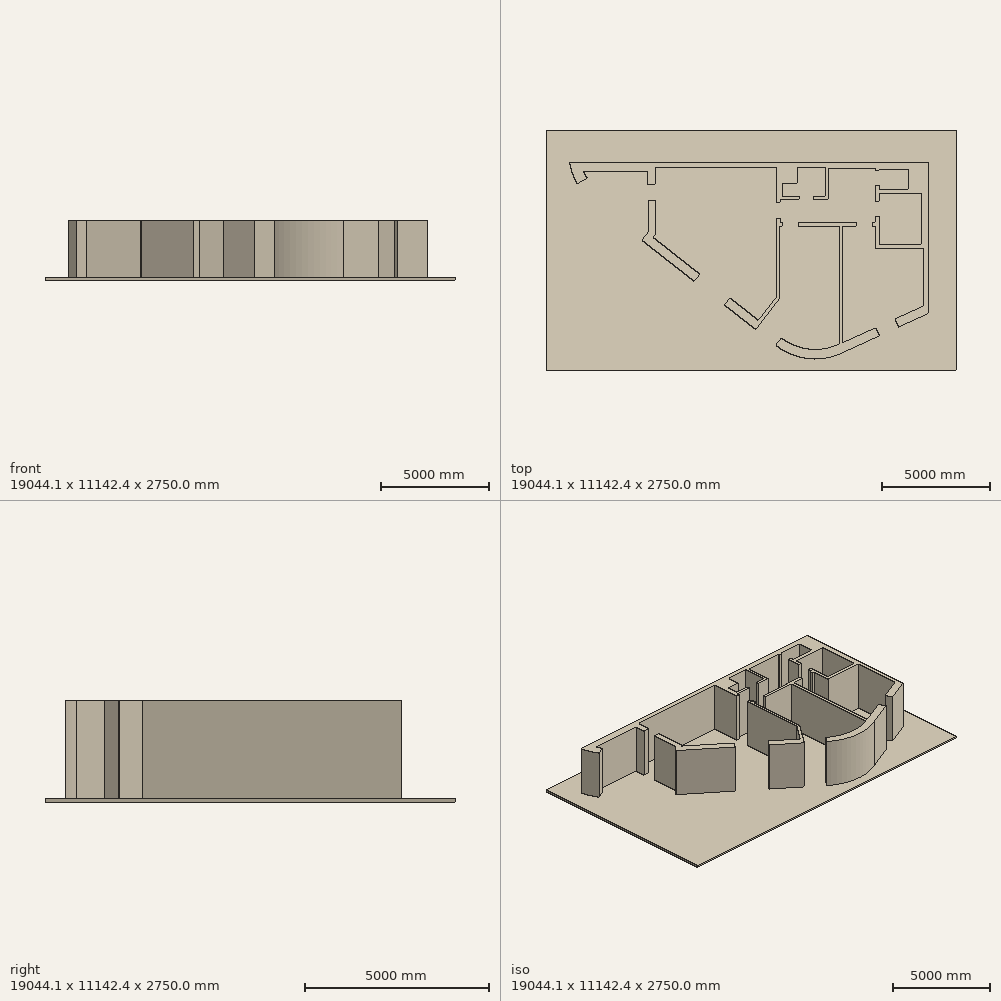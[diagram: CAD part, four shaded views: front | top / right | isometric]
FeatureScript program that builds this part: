
annotation { "Feature Type Name" : "Feature", "Feature Type Description" : "" }
export const myFeature = defineFeature(function(context is Context, id is Id, definition is map)
    precondition{}
    {
        {
            var Q0;
            Q0=qCreatedBy(makeId("Top.planeOp"),FACE);
            var sketch = newSketch(context, id + "F0", { "sketchPlane" : qUnion([Q0])});
            skLineSegment(sketch, "E0.bottom", {"start": v(-9332.98, 0) * mm, "end": v(-28377.12, 0) * mm});
            skLineSegment(sketch, "E0.top", {"start": v(-9332.98, 11142.35) * mm, "end": v(-28377.12, 11142.35) * mm});
            skLineSegment(sketch, "E0.left", {"start": v(-9332.98, 0) * mm, "end": v(-9332.98, 11142.35) * mm});
            skLineSegment(sketch, "E0.right", {"start": v(-28377.12, 0) * mm, "end": v(-28377.12, 11142.35) * mm});
            skSolve(sketch);
        }
        {
            var Q0;
            Q0=qCreatedBy(makeId("Top.planeOp"),FACE);
            var sketch = newSketch(context, id + "F1", { "sketchPlane" : qUnion([Q0])});
            skLineSegment(sketch, "E1", {"start": v(-17695.4, 9406.52) * mm, "end": v(-17695.4, 0) * mm, "construction": true});
            skLineSegment(sketch, "E2", {"start": v(-23335.4, 9420.42) * mm, "end": v(-23335.4, 0) * mm, "construction": true});
            skLineSegment(sketch, "E3", {"start": v(-26483.5, 8921.22) * mm, "end": v(-26661.71, 9232.56) * mm});
            skLineSegment(sketch, "E4", {"start": v(-26661.71, 9232.56) * mm, "end": v(-23679.3, 9232.56) * mm});
            skLineSegment(sketch, "E5", {"start": v(-23679.3, 9232.56) * mm, "end": v(-23679.3, 8644.23) * mm});
            skLineSegment(sketch, "E6", {"start": v(-23679.3, 8644.23) * mm, "end": v(-23335.4, 8644.23) * mm});
            skLineSegment(sketch, "E7", {"start": v(-23335.4, 8644.23) * mm, "end": v(-23335.4, 9420.42) * mm});
            skLineSegment(sketch, "E8", {"start": v(-23335.4, 9420.42) * mm, "end": v(-17884.5, 9420.42) * mm});
            skLineSegment(sketch, "E9", {"start": v(-17884.5, 9420.42) * mm, "end": v(-17695.4, 9420.42) * mm});
            skLineSegment(sketch, "E10", {"start": v(-26483.5, 8921.22) * mm, "end": v(-26938.35, 8660.86) * mm});
            skLineSegment(sketch, "E11", {"start": v(-23941.22, 6039.53) * mm, "end": v(-23657.8, 6399.56) * mm});
            skLineSegment(sketch, "E12", {"start": v(-23657.8, 6399.56) * mm, "end": v(-23657.8, 7903.53) * mm});
            skLineSegment(sketch, "E13", {"start": v(-23657.8, 7903.53) * mm, "end": v(-23335.4, 7903.53) * mm});
            skLineSegment(sketch, "E14", {"start": v(-23335.4, 7903.53) * mm, "end": v(-23335.4, 6259.12) * mm});
            skLineSegment(sketch, "E15", {"start": v(-23335.4, 6259.12) * mm, "end": v(-23412.66, 6169.75) * mm});
            skLineSegment(sketch, "E16", {"start": v(-23412.66, 6169.75) * mm, "end": v(-18525.74, 2320.29) * mm});
            skLineSegment(sketch, "E17", {"start": v(-18525.74, 2320.29) * mm, "end": v(-17695.4, 3390.84) * mm});
            skLineSegment(sketch, "E18", {"start": v(-17695.4, 3390.84) * mm, "end": v(-17695.4, 7043.86) * mm});
            skLineSegment(sketch, "E19", {"start": v(-17695.4, 7043.86) * mm, "end": v(-17529.29, 7043.86) * mm});
            skLineSegment(sketch, "E20", {"start": v(-17529.29, 7043.86) * mm, "end": v(-17529.29, 6860) * mm});
            skLineSegment(sketch, "E21", {"start": v(-17529.29, 6860) * mm, "end": v(-17434.81, 6860) * mm});
            skLineSegment(sketch, "E22", {"start": v(-17434.81, 6860) * mm, "end": v(-17434.81, 6678.72) * mm});
            skLineSegment(sketch, "E23", {"start": v(-17434.81, 6678.72) * mm, "end": v(-17531.84, 6678.72) * mm});
            skLineSegment(sketch, "E24", {"start": v(-17531.84, 6678.72) * mm, "end": v(-17531.84, 3343.08) * mm});
            skLineSegment(sketch, "E25", {"start": v(-17531.84, 3343.08) * mm, "end": v(-18647.56, 1890.31) * mm});
            skLineSegment(sketch, "E26", {"start": v(-18647.56, 1890.31) * mm, "end": v(-23941.22, 6039.53) * mm});
            skLineSegment(sketch, "E27", {"start": v(-17460.85, 1503.1) * mm, "end": v(-17728.59, 1163.2) * mm});
            skLineSegment(sketch, "E28", {"start": v(-14768.9, 6697.75) * mm, "end": v(-16661, 6697.75) * mm});
            skLineSegment(sketch, "E29", {"start": v(-16661, 6697.75) * mm, "end": v(-16661, 6850.95) * mm});
            skLineSegment(sketch, "E30", {"start": v(-16661, 6850.95) * mm, "end": v(-13976.46, 6865.49) * mm});
            skLineSegment(sketch, "E31", {"start": v(-13976.46, 6865.49) * mm, "end": v(-13975.51, 6690.41) * mm});
            skLineSegment(sketch, "E32", {"start": v(-13975.51, 6690.41) * mm, "end": v(-14608.4, 6690.41) * mm});
            skLineSegment(sketch, "E33", {"start": v(-14608.4, 6690.41) * mm, "end": v(-14608.4, 1282.42) * mm});
            skLineSegment(sketch, "E34", {"start": v(-14608.4, 1282.42) * mm, "end": v(-10858.67, 2988.86) * mm});
            skLineSegment(sketch, "E35", {"start": v(-10858.67, 2988.86) * mm, "end": v(-10858.67, 5686.8) * mm});
            skLineSegment(sketch, "E36", {"start": v(-10858.67, 5686.8) * mm, "end": v(-13106.53, 5686.8) * mm});
            skLineSegment(sketch, "E37", {"start": v(-13106.53, 5686.8) * mm, "end": v(-13106.53, 6690.41) * mm});
            skLineSegment(sketch, "E38", {"start": v(-13106.53, 6690.41) * mm, "end": v(-13212.43, 6690.41) * mm});
            skLineSegment(sketch, "E39", {"start": v(-13212.43, 6690.41) * mm, "end": v(-13212.43, 6866.77) * mm});
            skLineSegment(sketch, "E40", {"start": v(-13212.43, 6866.77) * mm, "end": v(-13094.97, 6866.77) * mm});
            skLineSegment(sketch, "E41", {"start": v(-13094.97, 6866.77) * mm, "end": v(-13094.97, 7134.88) * mm});
            skLineSegment(sketch, "E42", {"start": v(-13094.97, 7134.88) * mm, "end": v(-12918.79, 7134.88) * mm});
            skLineSegment(sketch, "E43", {"start": v(-12918.79, 7134.88) * mm, "end": v(-12918.79, 5870.93) * mm});
            skLineSegment(sketch, "E44", {"start": v(-12918.79, 5870.93) * mm, "end": v(-10960.3, 5870.93) * mm});
            skLineSegment(sketch, "E45", {"start": v(-10960.3, 5870.93) * mm, "end": v(-10960.3, 8217.53) * mm});
            skLineSegment(sketch, "E46", {"start": v(-10960.3, 8217.53) * mm, "end": v(-12926.45, 8217.53) * mm});
            skLineSegment(sketch, "E47", {"start": v(-12926.45, 8217.53) * mm, "end": v(-12926.45, 7847.28) * mm});
            skLineSegment(sketch, "E48", {"start": v(-12926.45, 7847.28) * mm, "end": v(-13094.97, 7847.28) * mm});
            skLineSegment(sketch, "E49", {"start": v(-13094.97, 7847.28) * mm, "end": v(-13094.97, 8592.88) * mm});
            skLineSegment(sketch, "E50", {"start": v(-13094.97, 8592.88) * mm, "end": v(-12923.9, 8592.88) * mm});
            skLineSegment(sketch, "E51", {"start": v(-12923.9, 8592.88) * mm, "end": v(-12923.9, 8409.04) * mm});
            skLineSegment(sketch, "E52", {"start": v(-12923.9, 8409.04) * mm, "end": v(-11542.5, 8409.04) * mm});
            skLineSegment(sketch, "E53", {"start": v(-11542.5, 8409.04) * mm, "end": v(-11542.5, 9343.6) * mm});
            skLineSegment(sketch, "E54", {"start": v(-11542.5, 9343.6) * mm, "end": v(-12923.9, 9343.6) * mm});
            skLineSegment(sketch, "E55", {"start": v(-12923.9, 9343.6) * mm, "end": v(-12923.9, 9266.99) * mm});
            skLineSegment(sketch, "E56", {"start": v(-12923.9, 9266.99) * mm, "end": v(-13094.97, 9266.99) * mm});
            skLineSegment(sketch, "E57", {"start": v(-13094.97, 9266.99) * mm, "end": v(-13094.97, 9358.71) * mm});
            skLineSegment(sketch, "E58", {"start": v(-13094.97, 9358.71) * mm, "end": v(-15261.57, 9358.71) * mm});
            skLineSegment(sketch, "E59", {"start": v(-15261.57, 9358.71) * mm, "end": v(-15261.57, 7945.19) * mm});
            skLineSegment(sketch, "E60", {"start": v(-15261.57, 7945.19) * mm, "end": v(-15980.18, 7945.19) * mm});
            skLineSegment(sketch, "E61", {"start": v(-15980.18, 7945.19) * mm, "end": v(-15980.18, 8091.44) * mm});
            skLineSegment(sketch, "E62", {"start": v(-15980.18, 8091.44) * mm, "end": v(-15427.68, 8091.44) * mm});
            skLineSegment(sketch, "E63", {"start": v(-15427.68, 8091.44) * mm, "end": v(-15427.68, 9413.1) * mm});
            skLineSegment(sketch, "E64", {"start": v(-15427.68, 9413.1) * mm, "end": v(-16707.82, 9413.1) * mm});
            skLineSegment(sketch, "E65", {"start": v(-16707.82, 9413.1) * mm, "end": v(-16707.82, 8705.32) * mm});
            skLineSegment(sketch, "E66", {"start": v(-16707.82, 8705.32) * mm, "end": v(-17417.4, 8705.32) * mm});
            skLineSegment(sketch, "E67", {"start": v(-17417.4, 8705.32) * mm, "end": v(-17417.4, 8082.4) * mm});
            skLineSegment(sketch, "E68", {"start": v(-17417.4, 8082.4) * mm, "end": v(-16637.4, 8082.4) * mm});
            skLineSegment(sketch, "E69", {"start": v(-16637.4, 8082.4) * mm, "end": v(-16637.4, 7937.96) * mm});
            skLineSegment(sketch, "E70", {"start": v(-16637.4, 7937.96) * mm, "end": v(-17529.29, 7937.96) * mm});
            skLineSegment(sketch, "E71", {"start": v(-17529.29, 7937.96) * mm, "end": v(-17529.29, 7817) * mm});
            skLineSegment(sketch, "E72", {"start": v(-17529.29, 7817) * mm, "end": v(-17695.4, 7817) * mm});
            skLineSegment(sketch, "E73", {"start": v(-17695.4, 7817) * mm, "end": v(-17695.4, 9420.42) * mm});
            skLineSegment(sketch, "E74", {"start": v(-26876.35, 9668.37) * mm, "end": v(-27302.77, 9668.37) * mm});
            skLineSegment(sketch, "E75", {"start": v(-26876.35, 9668.37) * mm, "end": v(-10618.17, 9668.37) * mm});
            skLineSegment(sketch, "E76", {"start": v(-10618.17, 9668.37) * mm, "end": v(-10618.17, 2643.46) * mm});
            skLineSegment(sketch, "E77", {"start": v(-10618.17, 2643.46) * mm, "end": v(-12042.04, 1997.46) * mm});
            skLineSegment(sketch, "E78", {"start": v(-12042.04, 1997.46) * mm, "end": v(-14546.78, 848.84) * mm});
            skArc(sketch, "E79", {"start": v(-17728.59, 1163.2) * mm, "mid": v(-16183.2, 545.32) * mm, "end": v(-14546.78, 848.84) * mm});
            skLineSegment(sketch, "E80", {"start": v(-14768.9, 6697.75) * mm, "end": v(-14768.9, 1221.92) * mm});
            skArc(sketch, "E81", {"start": v(-17460.85, 1503.1) * mm, "mid": v(-16153.97, 988.2) * mm, "end": v(-14768.9, 1221.92) * mm});
            skArc(sketch, "E82", {"start": v(-27302.77, 9668.37) * mm, "mid": v(-27172.75, 9145.74) * mm, "end": v(-26938.35, 8660.86) * mm});
            skLineSegment(sketch, "E83", {"start": v(-19845.02, 3359.5) * mm, "end": v(-20102.64, 3030.82) * mm});
            skLineSegment(sketch, "E84", {"start": v(-21505.64, 4130.5) * mm, "end": v(-21244.57, 4461.93) * mm});
            skLineSegment(sketch, "E85", {"start": v(-13080.52, 1977.73) * mm, "end": v(-12907.55, 1600.56) * mm});
            skLineSegment(sketch, "E86", {"start": v(-12186.32, 2384.67) * mm, "end": v(-12016, 2009.28) * mm});
            skSolve(sketch);
        }
        {
            var Q0;
            Q0=makeQuery(id+"F1.imprint","IMPRINT",FACE,{"disambiguationData":[TD([[makeQuery(id+"F1.imprint","IMPRINT",EDGE,{"derivedFrom":sQuery(id+"F1.wireOp",EDGE,"E3")}),1.0]])]});
            var Q1;
            {var subQ0=sQuery(id+"F1.wireOp",EDGE,"E11");Q1=makeQuery(id+"F1.imprint","IMPRINT",FACE,{"disambiguationData":[TD([[makeQuery(id+"F1.imprint","IMPRINT",EDGE,{"derivedFrom":subQ0}),-1.0]])]});}
            var Q2;
            {var subQ2=sQuery(id+"F1.wireOp",EDGE,"E17");Q2=makeQuery(id+"F1.imprint","IMPRINT",FACE,{"disambiguationData":[TD([[makeQuery(id+"F1.imprint","IMPRINT",EDGE,{"derivedFrom":subQ2}),-1.0]])]});}
            var Q3;
            Q3=makeQuery(id+"F1.imprint","IMPRINT",FACE,{"disambiguationData":[TD([[makeQuery(id+"F1.imprint","IMPRINT",EDGE,{"derivedFrom":sQuery(id+"F1.wireOp",EDGE,"E27")}),1.0]])]});
            extrude(context, id + "F2", {"entities" : qUnion([Q0, Q1, Q2, Q3]), "depth" : 2650 * mm, "offsetDistance" : 25 * mm});
        }
        {
            var Q0;
            Q0=makeQuery(id+"F0.imprint","IMPRINT",FACE,{"disambiguationData":[TD([[makeQuery(id+"F0.imprint","IMPRINT",EDGE,{"derivedFrom":sQuery(id+"F0.wireOp",EDGE,"E0.bottom")}),-1.0]])]});
            extrude(context, id + "F3", {"entities" : qUnion([Q0]), "oppositeDirection" : true, "depth" : 100 * mm, "offsetDistance" : 25 * mm});
        }
    });
